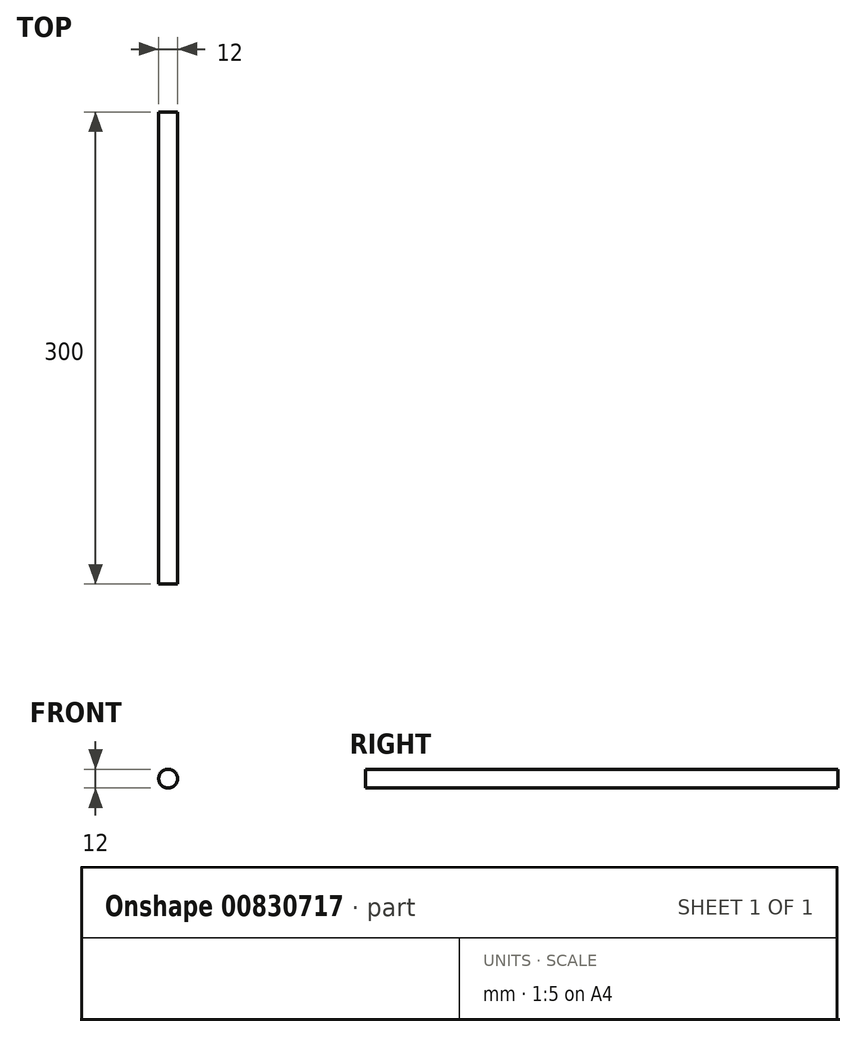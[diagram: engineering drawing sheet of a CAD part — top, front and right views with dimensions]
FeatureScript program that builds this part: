
annotation { "Feature Type Name" : "Feature", "Feature Type Description" : "" }
export const myFeature = defineFeature(function(context is Context, id is Id, definition is map)
    precondition{}
    {
        {
            var Q0;
            Q0=qCreatedBy(makeId("Front.planeOp"),FACE);
            var sketch = newSketch(context, id + "F0", { "sketchPlane" : qUnion([Q0])});
            skCircle(sketch, "E0", {"center": v(0, 0) * mm, "radius": 6 * mm});
            skSolve(sketch);
        }
        {
            var Q0;
            Q0=makeQuery(id+"F0.imprint","IMPRINT",FACE,{"disambiguationData":[TD([[makeQuery(id+"F0.imprint","IMPRINT",EDGE,{"derivedFrom":sQuery(id+"F0.wireOp",EDGE,"E0")}),1.0]])]});
            extrude(context, id + "F1", {"entities" : qUnion([Q0]), "depth" : 300 * mm, "offsetDistance" : 25 * mm});
        }
    });
